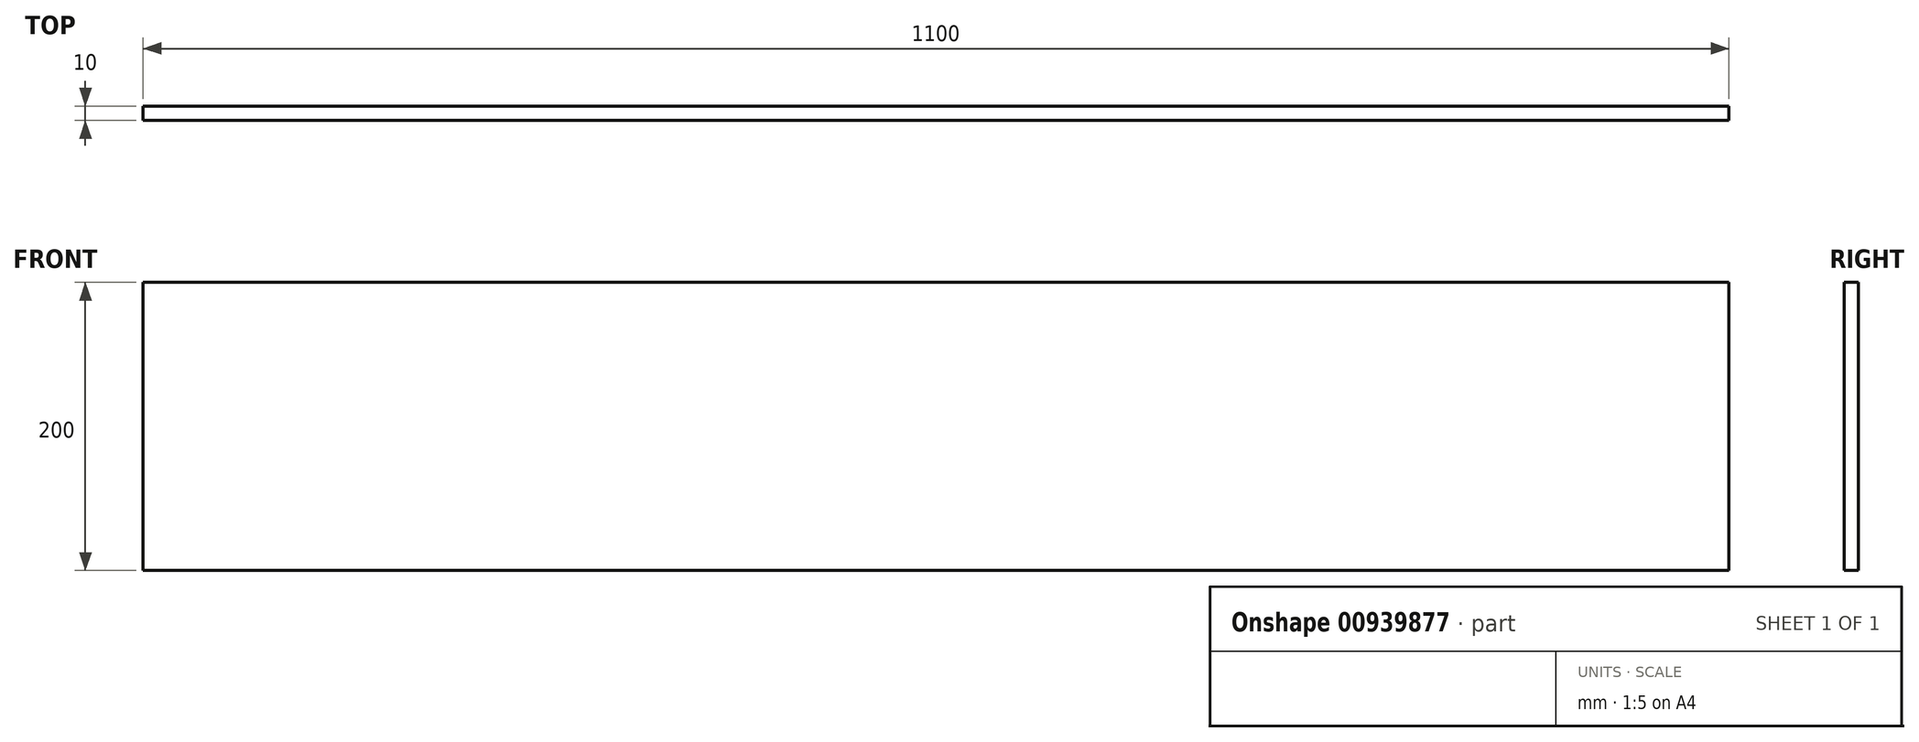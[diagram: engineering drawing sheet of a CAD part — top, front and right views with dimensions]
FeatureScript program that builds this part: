
annotation { "Feature Type Name" : "Feature", "Feature Type Description" : "" }
export const myFeature = defineFeature(function(context is Context, id is Id, definition is map)
    precondition{}
    {
        {
            var Q0;
            Q0=qCreatedBy(makeId("Front.planeOp"),FACE);
            var sketch = newSketch(context, id + "F0", { "sketchPlane" : qUnion([Q0])});
            skLineSegment(sketch, "E0.bottom", {"start": v(-550, 100) * mm, "end": v(550, 100) * mm});
            skLineSegment(sketch, "E0.top", {"start": v(-550, -100) * mm, "end": v(550, -100) * mm});
            skLineSegment(sketch, "E0.left", {"start": v(-550, 100) * mm, "end": v(-550, -100) * mm});
            skLineSegment(sketch, "E0.right", {"start": v(550, 100) * mm, "end": v(550, -100) * mm});
            skPoint(sketch, "E0.middle", {"position": v(0, 0) * mm});
            skSolve(sketch);
        }
        {
            var Q0;
            Q0=makeQuery(id+"F0.imprint","IMPRINT",FACE,{"disambiguationData":[TD([[makeQuery(id+"F0.imprint","IMPRINT",EDGE,{"derivedFrom":sQuery(id+"F0.wireOp",EDGE,"E0.bottom")}),-1.0]])]});
            extrude(context, id + "F1", {"entities" : qUnion([Q0]), "depth" : 10 * mm, "offsetDistance" : 25 * mm});
        }
    });
